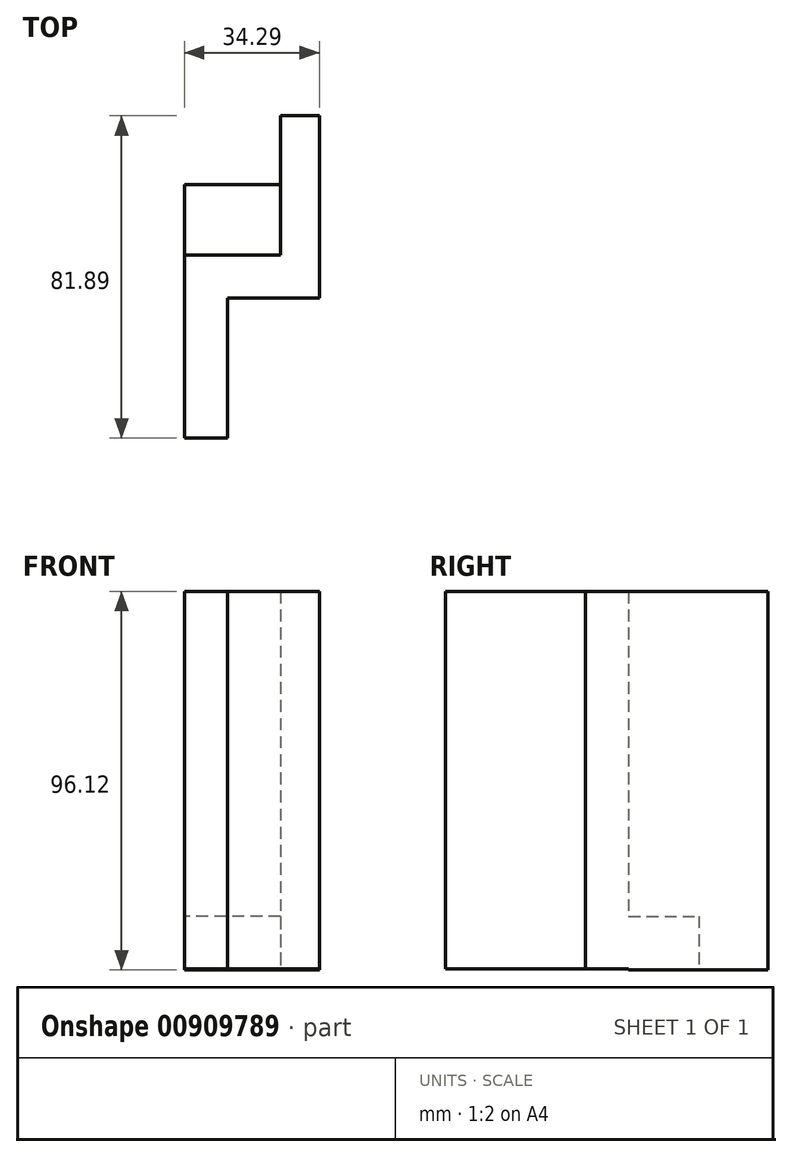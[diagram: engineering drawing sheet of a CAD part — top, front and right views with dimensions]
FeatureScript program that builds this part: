
annotation { "Feature Type Name" : "Feature", "Feature Type Description" : "" }
export const myFeature = defineFeature(function(context is Context, id is Id, definition is map)
    precondition{}
    {
        {
            var Q0;
            Q0=qCreatedBy(makeId("Right.planeOp"),FACE);
            var sketch = newSketch(context, id + "F0", { "sketchPlane" : qUnion([Q0])});
            skLineSegment(sketch, "E0.bottom", {"start": v(-46.53, 55.7) * mm, "end": v(0, 55.7) * mm});
            skLineSegment(sketch, "E0.top", {"start": v(-46.53, -40.14) * mm, "end": v(0, -40.14) * mm});
            skLineSegment(sketch, "E0.left", {"start": v(-46.53, 55.7) * mm, "end": v(-46.53, -40.14) * mm});
            skLineSegment(sketch, "E0.right", {"start": v(0, 55.7) * mm, "end": v(0, -40.14) * mm});
            skLineSegment(sketch, "E1.bottom", {"start": v(0, -26.8) * mm, "end": v(17.92, -26.8) * mm});
            skLineSegment(sketch, "E1.top", {"start": v(0, -40.42) * mm, "end": v(17.92, -40.42) * mm});
            skLineSegment(sketch, "E1.left", {"start": v(0, -26.8) * mm, "end": v(0, -40.42) * mm});
            skLineSegment(sketch, "E1.right", {"start": v(17.92, -26.8) * mm, "end": v(17.92, -40.42) * mm});
            skSolve(sketch);
        }
        {
            var Q0;
            Q0=makeQuery(id+"F0.imprint","IMPRINT",FACE,{"disambiguationData":[TD([[makeQuery(id+"F0.imprint","IMPRINT",EDGE,{"derivedFrom":sQuery(id+"F0.wireOp",EDGE,"E0.bottom")}),-1.0]])]});
            var Q1;
            {var subQ3=sQuery(id+"F0.wireOp",EDGE,"E1.bottom");Q1=makeQuery(id+"F0.imprint","IMPRINT",FACE,{"disambiguationData":[TD([[makeQuery(id+"F0.imprint","IMPRINT",EDGE,{"derivedFrom":subQ3}),-1.0]])]});}
            extrude(context, id + "F1", {"entities" : qUnion([Q0, Q1]), "depth" : 10.92 * mm, "offsetDistance" : 25.4 * mm});
        }
        {
            var Q0;
            Q0=makeQuery(id+"F1.opExtrude","CAP_FACE",FACE,{"disambiguationData":[OSD([sQuery(id+"F0.wireOp",EDGE,"E0.bottom"),sQuery(id+"F0.wireOp",EDGE,"E0.top"),sQuery(id+"F0.wireOp",EDGE,"E0.left"),sQuery(id+"F0.wireOp",EDGE,"E0.right"),sQuery(id+"F0.wireOp",EDGE,"E1.bottom"),sQuery(id+"F0.wireOp",EDGE,"E1.top"),sQuery(id+"F0.wireOp",EDGE,"E1.left"),sQuery(id+"F0.wireOp",EDGE,"E1.right")])],"isStart":false});
            var sketch = newSketch(context, id + "F2", { "sketchPlane" : qUnion([Q0])});
            skLineSegment(sketch, "E2.bottom", {"start": v(-10.96, 55.7) * mm, "end": v(0, 55.7) * mm});
            skLineSegment(sketch, "E2.top", {"start": v(-10.96, -40.14) * mm, "end": v(0, -40.14) * mm});
            skLineSegment(sketch, "E2.left", {"start": v(-10.96, 55.7) * mm, "end": v(-10.96, -40.14) * mm});
            skLineSegment(sketch, "E2.right", {"start": v(0, 55.7) * mm, "end": v(0, -40.14) * mm});
            skLineSegment(sketch, "E3.bottom", {"start": v(0, -26.8) * mm, "end": v(17.92, -26.8) * mm});
            skLineSegment(sketch, "E3.top", {"start": v(0, -40.42) * mm, "end": v(17.92, -40.42) * mm});
            skLineSegment(sketch, "E3.left", {"start": v(0, -26.8) * mm, "end": v(0, -40.42) * mm});
            skLineSegment(sketch, "E3.right", {"start": v(17.92, -26.8) * mm, "end": v(17.92, -40.42) * mm});
            skSolve(sketch);
        }
        {
            var Q0;
            {var subQ1=sQuery(id+"F2.wireOp",EDGE,"E2.bottom");Q0=makeQuery(id+"F2.imprint","IMPRINT",FACE,{"disambiguationData":[TD([[makeQuery(id+"F2.imprint","IMPRINT",EDGE,{"derivedFrom":subQ1}),-1.0]])]});}
            var Q1;
            {var subQ3=sQuery(id+"F2.wireOp",EDGE,"E3.bottom");Q1=makeQuery(id+"F2.imprint","IMPRINT",FACE,{"disambiguationData":[TD([[makeQuery(id+"F2.imprint","IMPRINT",EDGE,{"derivedFrom":subQ3}),-1.0]])]});}
            extrude(context, id + "F3", {"entities" : qUnion([Q0, Q1]), "operationType" : NewBodyOperationType.ADD, "depth" : 13.46 * mm, "offsetDistance" : 25.4 * mm});
        }
        {
            var Q0;
            Q0=makeQuery(id+"F3.opExtrude","CAP_FACE",FACE,{"disambiguationData":[OSD([sQuery(id+"F2.wireOp",EDGE,"E2.bottom"),sQuery(id+"F2.wireOp",EDGE,"E2.top"),sQuery(id+"F2.wireOp",EDGE,"E2.left"),sQuery(id+"F2.wireOp",EDGE,"E2.right"),sQuery(id+"F2.wireOp",EDGE,"E3.bottom"),sQuery(id+"F2.wireOp",EDGE,"E3.top"),sQuery(id+"F2.wireOp",EDGE,"E3.left"),sQuery(id+"F2.wireOp",EDGE,"E3.right")])],"isStart":false});
            var sketch = newSketch(context, id + "F4", { "sketchPlane" : qUnion([Q0])});
            skLineSegment(sketch, "E4.bottom", {"start": v(-10.96, 55.7) * mm, "end": v(35.36, 55.7) * mm});
            skLineSegment(sketch, "E4.top", {"start": v(-10.96, -40.42) * mm, "end": v(35.36, -40.42) * mm});
            skLineSegment(sketch, "E4.left", {"start": v(-10.96, 55.7) * mm, "end": v(-10.96, -40.42) * mm});
            skLineSegment(sketch, "E4.right", {"start": v(35.36, 55.7) * mm, "end": v(35.36, -40.42) * mm});
            skSolve(sketch);
        }
        {
            var Q0;
            {var subQ0=sQuery(id+"F4.wireOp",EDGE,"E4.right");Q0=makeQuery(id+"F4.imprint","IMPRINT",FACE,{"disambiguationData":[TD([[makeQuery(id+"F4.imprint","IMPRINT",EDGE,{"derivedFrom":subQ0}),-1.0]])]});}
            var Q1;
            {var subQ3=makeQuery(id+"F3.opExtrude","CAP_EDGE",EDGE,{"disambiguationData":[OSD([sQuery(id+"F2.wireOp",EDGE,"E2.top")])],"isStart":false});Q1=makeQuery(id+"F4.imprint","IMPRINT",FACE,{"disambiguationData":[TD([[makeQuery(id+"F4.imprint","IMPRINT",EDGE,{"derivedFrom":subQ3}),1.0]])]});}
            extrude(context, id + "F5", {"entities" : qUnion([Q0, Q1]), "operationType" : NewBodyOperationType.ADD, "depth" : 9.9 * mm, "offsetDistance" : 25.4 * mm});
        }
    });
